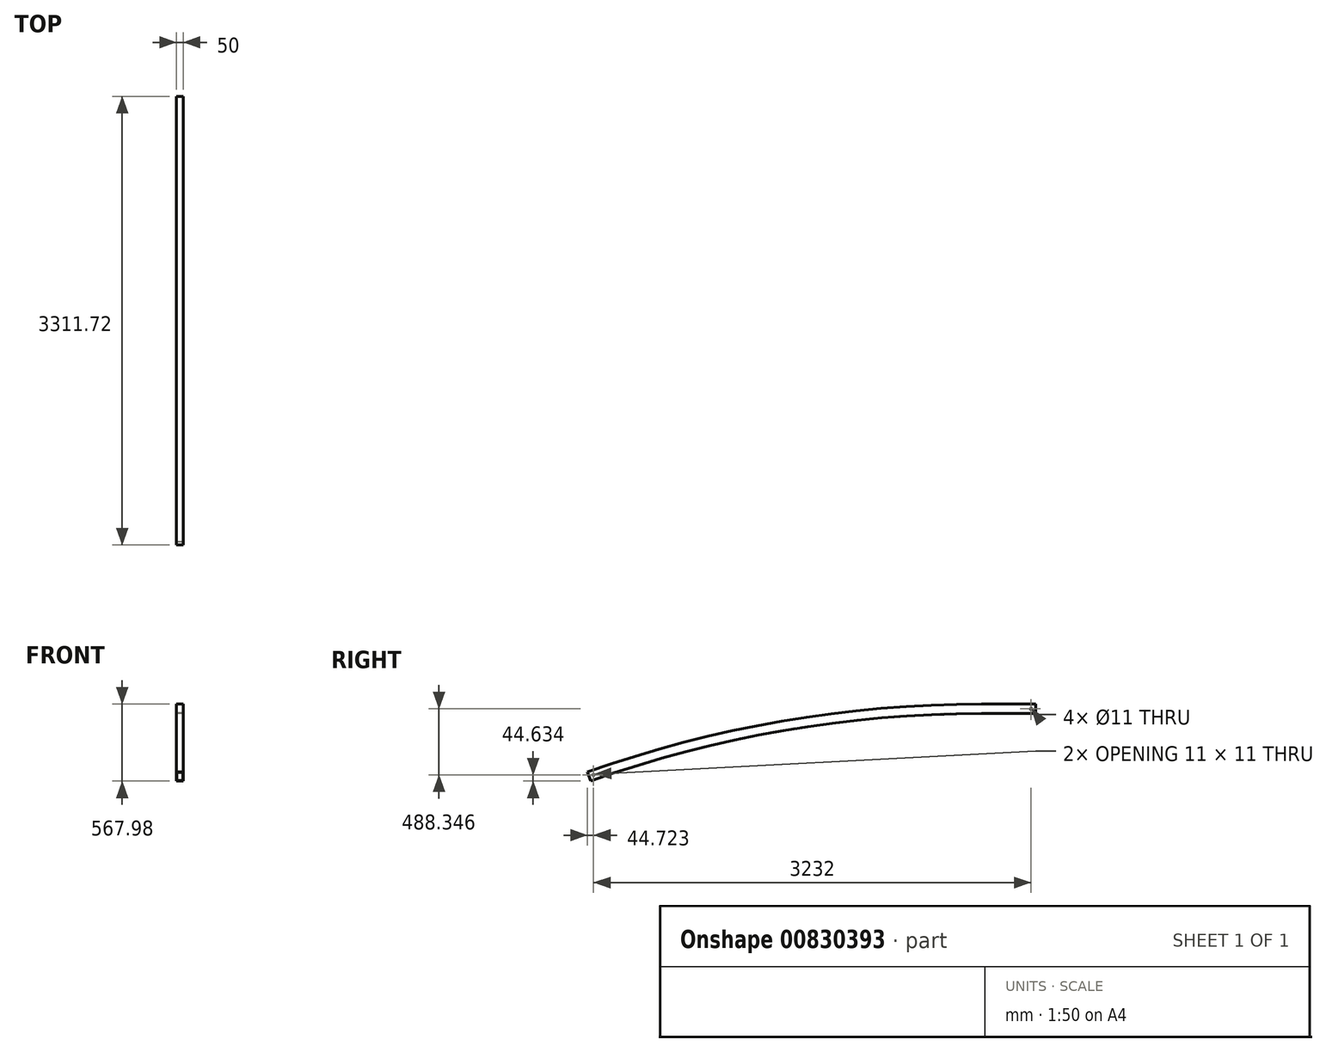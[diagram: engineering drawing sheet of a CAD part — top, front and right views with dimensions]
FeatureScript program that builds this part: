
annotation { "Feature Type Name" : "Feature", "Feature Type Description" : "" }
export const myFeature = defineFeature(function(context is Context, id is Id, definition is map)
    precondition{}
    {
        {
            var Q0;
            Q0=qCreatedBy(makeId("Front.planeOp"),FACE);
            var sketch = newSketch(context, id + "F0", { "sketchPlane" : qUnion([Q0])});
            skLineSegment(sketch, "E0.bottom", {"start": v(25, 35) * mm, "end": v(-25, 35) * mm});
            skLineSegment(sketch, "E0.top", {"start": v(25, -35) * mm, "end": v(-25, -35) * mm});
            skLineSegment(sketch, "E0.left", {"start": v(25, 35) * mm, "end": v(25, -35) * mm});
            skLineSegment(sketch, "E0.right", {"start": v(-25, 35) * mm, "end": v(-25, -35) * mm});
            skPoint(sketch, "E0.middle", {"position": v(0, 0) * mm});
            skLineSegment(sketch, "E1.0", {"start": v(-22, 32) * mm, "end": v(-22, -32) * mm});
            skLineSegment(sketch, "E1.1", {"start": v(22, 32) * mm, "end": v(-22, 32) * mm});
            skLineSegment(sketch, "E1.2", {"start": v(22, 32) * mm, "end": v(22, -32) * mm});
            skLineSegment(sketch, "E1.3", {"start": v(22, -32) * mm, "end": v(-22, -32) * mm});
            skSolve(sketch);
        }
        {
            var Q0;
            Q0=qCreatedBy(makeId("Right.planeOp"),FACE);
            var sketch = newSketch(context, id + "F1", { "sketchPlane" : qUnion([Q0])});
            skLineSegment(sketch, "E2", {"start": v(0, 0) * mm, "end": v(-400, 0) * mm});
            skLineSegment(sketch, "E3", {"start": v(0, 0) * mm, "end": v(-3300, 0) * mm, "construction": true});
            skLineSegment(sketch, "E4", {"start": v(-3300, 0) * mm, "end": v(-3300, -500) * mm, "construction": true});
            skArc(sketch, "E5", {"start": v(-400, 0) * mm, "mid": v(-1871.4, -125.92) * mm, "end": v(-3300, -500) * mm});
            skSolve(sketch);
        }
        {
            var Q0;
            Q0 = qSketchRegion(id + "F0", true);
            var Q1;
            Q1 = qConstructionFilter(qBodyType(qCreatedBy(id + "F1" ,EDGE), BodyType.WIRE), ConstructionObject.NO);
            sweep(context, id + "F2", {"profiles" : qUnion([Q0]), "path" : qUnion([Q1])});
        }
        {
            var Q0;
            Q0=makeQuery(id+"F2.opSweep","SWEPT_FACE",FACE,{"disambiguationData":[OSD([sQuery(id+"F0.wireOp",EDGE,"E0.right"),sQuery(id+"F1.wireOp",EDGE,"E5")])]});
            var sketch = newSketch(context, id + "F3", { "sketchPlane" : qUnion([Q0])});
            skPoint(sketch, "E6", {"position": v(35, 0) * mm});
            skPoint(sketch, "E7", {"position": v(3267, -488.35) * mm});
            skSolve(sketch);
        }
        {
            var Q0;
            Q0=sQuery(id+"F3.wireOp",VERTEX,"E7");
            var Q1;
            Q1=makeQuery(id+"F2.opSweep","SWEPT_BODY",BODY,{"disambiguationData":[OSD([sQuery(id+"F0.wireOp",EDGE,"E0.bottom"),sQuery(id+"F0.wireOp",EDGE,"E0.top"),sQuery(id+"F0.wireOp",EDGE,"E0.left"),sQuery(id+"F0.wireOp",EDGE,"E0.right"),sQuery(id+"F0.wireOp",EDGE,"E1.0"),sQuery(id+"F0.wireOp",EDGE,"E1.1"),sQuery(id+"F0.wireOp",EDGE,"E1.2"),sQuery(id+"F0.wireOp",EDGE,"E1.3"),sQuery(id+"F1.wireOp",EDGE,"E5")])]});
            hole(context, id + "F4", {"style" : HoleStyle.SIMPLE, "endStyle" : HoleEndStyle.THROUGH, "holeDiameter" : 11 * mm, "majorDiameter" : 5 * mm, "isTappedThrough" : true, "tappedDepth" : 12 * mm, "tapClearance" : 3, "locations" : qUnion([Q0]), "scope" : qUnion([Q1])});
        }
        {
            var Q0;
            Q0=sQuery(id+"F3.wireOp",VERTEX,"E6");
            var Q1;
            Q1=makeQuery(id+"F2.opSweep","SWEPT_BODY",BODY,{"disambiguationData":[OSD([sQuery(id+"F0.wireOp",EDGE,"E0.bottom"),sQuery(id+"F0.wireOp",EDGE,"E0.top"),sQuery(id+"F0.wireOp",EDGE,"E0.left"),sQuery(id+"F0.wireOp",EDGE,"E0.right"),sQuery(id+"F0.wireOp",EDGE,"E1.0"),sQuery(id+"F0.wireOp",EDGE,"E1.1"),sQuery(id+"F0.wireOp",EDGE,"E1.2"),sQuery(id+"F0.wireOp",EDGE,"E1.3"),sQuery(id+"F1.wireOp",EDGE,"E5")])]});
            hole(context, id + "F5", {"style" : HoleStyle.SIMPLE, "endStyle" : HoleEndStyle.THROUGH, "holeDiameter" : 11 * mm, "majorDiameter" : 5 * mm, "isTappedThrough" : true, "tappedDepth" : 12 * mm, "tapClearance" : 3, "locations" : qUnion([Q0]), "scope" : qUnion([Q1])});
        }
    });
